# Revit family: Food-Service-Equipment_Oscartek_Ps1200_Curved-Glass
name_source: partatom
category: Specialty Equipment
units: mm (PartAtom-declared; Revit-internal decimal feet)

## family parameters
Always vertical = Yes
Classification Number = 23.40.40.11
Cut with Voids When Loaded = No
Enable Cutting in Views = No
Maintain Annotation Orientation = No
Part Type = Normal
Room Calculation Point = No
Round Connector Dimension = Use Diameter
Shared = No
Work Plane-Based = No

## types (1)
- Food-Service-Equipment_Oscartek_Ps1200_Curved-Glass
    Apparent Power = 480 VA
    Building Codes = https://www.arcat.com
    CSI Master Format = Foodservice Shelving
    CSI MasterFormat = 11 41 33
    Conn Conduit = Yes
    Construction Details = http://www.oscartek.com
    Cycle = 60 Hz
    Default Elevation = 0"
    Depth = 37 5/8"
    Description = PREP STATION CURVE GLASS SNEEZE GUARD
    FL Amps = 4 A
    Green Building-LEED = https://www.arcat.com
    Height = 40 11/16"
    Indirect Waste Connection Height = 0"
    Indirect Waste Flow = 0 GPM
    Indirect Waste Size = 0"
    Installation-Fabrication = http://www.oscartek.com
    Manufacturer = OSCARTEK
    Manufacturer Fax = 650-342-7400
    Manufacturer Website = http://www.oscartek.com
    Max Overcurrent Protection = 0 A
    Min Ckt Ampacity = 0 A
    Model = PS1200
    Phase = 1
    Product Data = http://www.oscartek.com
    Revision = R1_2018-10
    Sales Information = http://www.oscartek.com
    Specification = https://www.arcat.com
    Test Data = http://www.oscartek.com
    Type Comments = As Specified
    URL = www.oscartek.com
    URL Cutsheet = www.oscartek.com
    Volts = 120 V
    Watts = 480 W
    Weight in Pounds = 0
    Width = 48"

## geometry (parser evidence)
native form markers: Blend x44, Sweep x3
no freeform markers — native parametric forms only
